# Revit family: kleine_glocke___st1_2a_5xa1573k1b108_5058
name_source: partatom
category: Lighting Fixtures
units: mm (PartAtom-declared; Revit-internal decimal feet)

## family parameters
Cut with Voids When Loaded = No
Host = Face
Light Source = No
Part Type = Normal
Room Calculation Point = No
Round Connector Dimension = Use Diameter
Shared = No

## types (1)
- --- (1 x LED, 1730 lm, 13.2 W, 4000K)
    Apparent Load = 13 VA
    CIE Flux Codes = 28 65 95 99 100
    Color Rendering = 70
    Color Temperature = 4000K
    Default Elevation = 1800 mm
    Description = Small Bell, mast luminaire, primary light control with 3 zone facetted reflector, of plastic, aluminium vaporised, primary optical cover: enclosure, of PMMA, transparent, light distribution: ST1.2a, light emission: direct distribution, primary light characteristic: asymmetric, installation type: suspended mounting, LED, High Power LED, rated luminous flux: 1.730lm, luminous efficacy: 131lm/W, light colour: 740, colour temperature: 4000K, control gear: ECG Plus, control: flexible luminous flux parameterisation, time-dependent luminous flux control, constant luminous flux control, digital communication interface, power reduction, electronic power reduction, mains connection: 230..240V, AC, 50/60Hz, start of lifetime: 13W, end of service life: 14W, reduction: 7W, luminaire housing, bell-shaped, of glass-fibre reinforced polyester, coated, Siteco® metallic grey (DB 702S), please order curved mast extension separately, diameter: 430mm, height: 575mm, protection rating (complete): IP54, insulation class (complete): insulation class II (safety insulation), certification: CE, ENEC, VDE, impact resistance: IK09, standard-compliant lighting for roads and squares, packaging unit: 1 piece

Light Distribution: ST1.2a
    Height = 575 mm
    Lamp = 1 x LED
    Lamp Light Flux = 1730 lm
    Lamp Power = 13.2 W
    Lamp count = 1
    Length = 430 mm
    Luminous efficacy = 131 lm/W
    Manufacturer = Siteco
    ModVariant = No
    Model = 5XA1573K1B108
    Number of Poles = 1
    OnlyDefault = Yes
    Power Factor = 1
    Product Name = Kleine Glocke | ST1.2a
    Product group = mast luminaire | pylon annexe
    ProductGroupID = 6201
    Protection Class = Protection class II
    Protection Degree = IP 54
    RLX_Detail_Level = 1
    RLX_Emergency_Light_Flux = 0 lm
    RLX_Emergency_Type = 0
    RLX_Emergency_Type_DB = No
    RlxData = <blob elided: 50641 chars, md5=bbc28d1c>
    Socket = socket
    Standby Power = 0 W
    System Light Flux = 1730 lm
    System Power = 13 W
    Type Comments = factory setting: luminous flux: 100 % | dim-lin: 254 | 249 mA
    Type Image = l_1284396.jpg
    URL = http://relux.com
    VarID = @adj_154339
    Voltage = 0 V
    Weight = 0.00 kg
    Width = 0 mm  [stored 0 ft]

note: [stored X ft] marks values corroborated as IEEE doubles in the binary element streams (Revit-internal decimal feet)

## geometry (parser evidence)
native form markers: Sweep x10
no freeform markers — native parametric forms only
